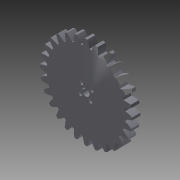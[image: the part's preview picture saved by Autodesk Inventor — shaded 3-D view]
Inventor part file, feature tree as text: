
AUTODESK INVENTOR PART (.ipt)
format: ipt  version: 2015 (Build 190159000, 159)  size: 242,176 bytes
history: native  units: mm (DEFAULTED — no unit token found)
features: plane x3, other x3, sketch x3, extrude x2
ambient origin geometry x8: Origin, YZ Plane, XZ Plane, XY Plane, X Axis, Y Axis, Z Axis, Center Point
bodies: Solid1 (feature_tree)
feature tree (11):
  extrude  "Extrusion1"  Depth=8.89mm TaperAngle=0.0deg
  plane  "Work Plane1"
  plane  "Work Plane2"
  plane  "Work Plane3"
  other  "Spur Gear"
  extrude  "Extrusion2"  Depth=76.2mm TaperAngle=0.0deg
  sketch  "Sketch1"  dims[d0=101.6mm d1=8.89mm d2=0.0mm]
  sketch  "Sketch2"  dims[d3=94.826667mm d4=76.2mm d5=0.0mm]
  other  "Srf1"
  sketch  "Sketch3"  dims[d6=0.0mm d7=1.121997mm d9=0.0mm d14=0.0mm d15=96.52mm d16=0.0mm d17=0.0mm d18=0.0mm d19=96.52mm d20=25.4mm d21=0.0mm]
  other  "Pitch Diameter"
